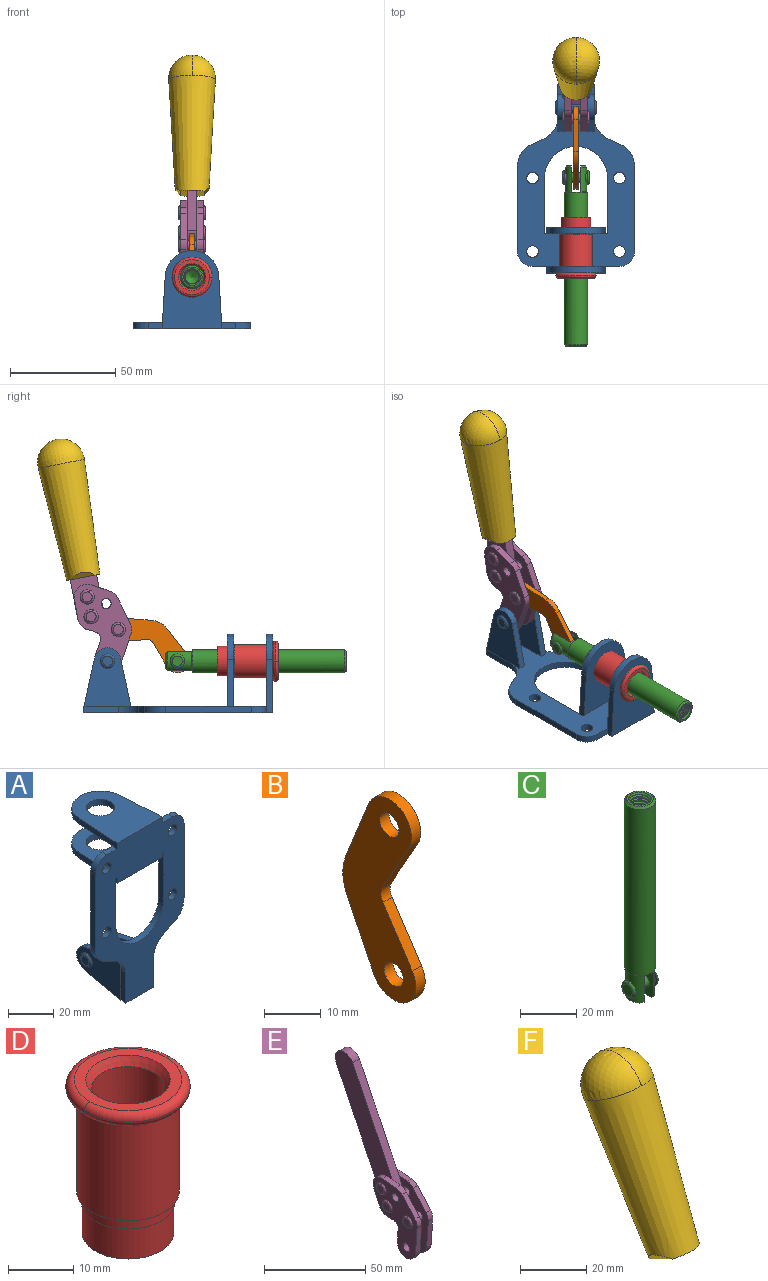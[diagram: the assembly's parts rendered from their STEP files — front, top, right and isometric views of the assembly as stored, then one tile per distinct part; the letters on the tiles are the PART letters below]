
ASSEMBLY  parts=6 mates=6
PART A: 55 faces, bbox 55.7x37.4x89.8 mm
  f0: torus R=2.41mm, axis (-1,0,0), area 15mm2, adj f11,f15,f25
  f1: torus R=2.41mm, axis (-1,0,0), area 15mm2, adj f10,f12,f22
  f2: cylinder r=2.78mm len=5.56mm, axis (0,-1,0), area 54.2mm2, adj f30,f54
  f3: cylinder r=14.99mm len=29.97mm, axis (0,-1,0), area 145.9mm2, adj f30,f49,f53,f54
  f4: cylinder r=2.78mm len=5.56mm, axis (0,-1,0), area 54.2mm2, adj f30,f54
  f5: cylinder r=2.78mm len=5.56mm, axis (0,-1,0), area 54.2mm2, adj f30,f54
  f6: cylinder r=2.78mm len=5.56mm, axis (0,-1,0), area 54.2mm2, adj f30,f54
  f7: cylinder r=6.35mm len=12.7mm, axis (0,0,1), area 123.6mm2, adj f27,f51
  f8: cylinder r=6.35mm len=12.7mm, axis (0,0,-1), area 124.7mm2, adj f21,f35
  f9: cylinder r=2.41mm len=11.18mm, axis (-1,0,0), area 169.4mm2, adj f16,f19
  f10: plane 4.83x4.83mm, normal (1,0,0), area 18.3mm2, adj f1,f12
  f11: plane 4.83x4.83mm, normal (-1,0,0), area 18.3mm2, adj f0,f15
  f12: torus R=2.41mm, axis (-1,0,0), area 15mm2, adj f1,f10,f22
  f13: cylinder r=6.35mm len=12.41mm, axis (1,0,0), area 53.4mm2, adj f18,f19,f22,f23
  f14: cylinder r=6.35mm len=12.41mm, axis (-1,0,0), area 53.4mm2, adj f16,f17,f24,f25
  f15: torus R=2.41mm, axis (-1,0,0), area 15mm2, adj f0,f11,f25
  f16: plane 27.86x22.35mm, normal (1,0,0), area 425.4mm2, adj f9,f14,f17,f24,f30
  f17: plane 22.86x4.97mm, normal (0,0.21,0.98), area 72.5mm2, adj f14,f16,f25,f30
  f18: plane 22.86x4.97mm, normal (0,0.21,0.98), area 72.5mm2, adj f13,f19,f22,f30
  f19: plane 27.86x22.35mm, normal (-1,0,0), area 425.4mm2, adj f9,f13,f18,f23,f30
  f20: cylinder r=12.7mm len=25.35mm, axis (0,0,-1), area 119.8mm2, adj f21,f34,f35,f36
  f21: plane 34.21x28.07mm, normal (0,0,-1), area 702.4mm2, adj f8,f20,f30,f34,f36
  f22: plane 27.96x22.45mm, normal (1,0,0), area 407.2mm2, adj f1,f12,f13,f18,f23,f30,f42,f43
  f23: plane 22.86x4.97mm, normal (0,0.21,-0.98), area 72.5mm2, adj f13,f19,f22,f44
  f24: plane 22.86x4.97mm, normal (0,0.21,-0.98), area 72.5mm2, adj f14,f16,f25,f44
  f25: plane 27.86x22.35mm, normal (-1,0,0), area 407.1mm2, adj f0,f14,f15,f17,f24,f30,f45,f46
  f26: plane 3.1x0.95mm, normal (0,0,-1), area 2.7mm2, adj f30,f49,f50,f54
  f27: plane 34.21x28.07mm, normal (0,0,1), area 702.4mm2, adj f7,f28,f30,f50,f52
  f28: cylinder r=12.7mm len=25.35mm, axis (0,0,1), area 118.8mm2, adj f27,f50,f51,f52
  f29: plane 3.1x0.95mm, normal (0,0,-1), area 2.7mm2, adj f30,f52,f53,f54
  f30: plane 86.54x55.63mm, normal (0,1,0), area 2362.9mm2, adj f2,f3,f4,f5,f6,f16,f17,f18
  f31: plane 40.56x3.1mm, normal (-1,0,0), area 125.7mm2, adj f30,f32,f48,f54
  f32: cylinder r=7.11mm len=7.11mm, axis (0,-1,0), area 34.6mm2, adj f30,f31,f33,f54
  f33: plane 6.67x3.1mm, normal (0,0,1), area 20.4mm2, adj f30,f32,f34,f54
  f34: plane 25.39x3.13mm, normal (-1,0.06,0), area 79.5mm2, adj f20,f21,f33,f35,f54
  f35: plane 37.31x28.45mm, normal (0,0,1), area 789.9mm2, adj f8,f20,f34,f36,f54
  f36: plane 25.39x3.13mm, normal (1,0.06,0), area 79.5mm2, adj f20,f21,f35,f37,f54
  f37: plane 6.67x3.1mm, normal (0,0,1), area 20.4mm2, adj f30,f36,f38,f54
  f38: cylinder r=7.11mm len=7.11mm, axis (0,-1,0), area 34.6mm2, adj f30,f37,f39,f54
  f39: plane 40.56x3.1mm, normal (1,0,0), area 125.7mm2, adj f30,f38,f40,f54
  f40: cylinder r=11.18mm len=10.16mm, axis (0,-1,0), area 39.5mm2, adj f30,f39,f41,f54
  f41: plane 6.09x3.1mm, normal (0.42,0,-0.91), area 20.8mm2, adj f30,f40,f42,f54
  f42: cylinder r=11.18mm len=9.41mm, axis (0,-1,0), area 37.2mm2, adj f22,f30,f41,f43,f54
  f43: plane 16.5x3.1mm, normal (1,0,0), area 51.1mm2, adj f22,f42,f44,f54
  f44: plane 17.37x3.1mm, normal (0,0,-1), area 53.8mm2, adj f23,f24,f30,f43,f45,f54
  f45: plane 16.5x3.1mm, normal (-1,0,0), area 51.1mm2, adj f25,f44,f46,f54
  f46: cylinder r=11.18mm len=9.41mm, axis (0,-1,0), area 37.2mm2, adj f25,f30,f45,f47,f54
  f47: plane 6.09x3.1mm, normal (-0.42,0,-0.91), area 20.8mm2, adj f30,f46,f48,f54
  f48: cylinder r=11.18mm len=10.16mm, axis (0,-1,0), area 39.5mm2, adj f30,f31,f47,f54
  f49: plane 26.54x3.1mm, normal (-1,0,0), area 82.3mm2, adj f3,f26,f30,f54
  f50: plane 25.39x3.1mm, normal (1,0.06,0), area 78.8mm2, adj f26,f27,f28,f51,f54
  f51: plane 37.31x28.45mm, normal (0,0,-1), area 789.9mm2, adj f7,f28,f50,f52,f54
  f52: plane 25.39x3.1mm, normal (-1,0.06,0), area 78.8mm2, adj f27,f28,f29,f51,f54
  f53: plane 26.54x3.1mm, normal (1,0,0), area 82.3mm2, adj f3,f29,f30,f54
  f54: plane 89.66x55.63mm, normal (0,-1,0), area 2678.5mm2, adj f2,f3,f4,f5,f6,f26,f29,f31
PART B: 12 faces, bbox 2.3x18.2x42.8 mm
  f0: cylinder r=2.4mm len=4.8mm, axis (1,0,0), area 34.9mm2, adj f4,f11
  f1: cylinder r=10.41mm len=8.47mm, axis (1,0,0), area 20.2mm2, adj f4,f9,f10,f11
  f2: cylinder r=3.05mm len=3.16mm, axis (1,0,0), area 7.7mm2, adj f4,f6,f7,f11
  f3: cylinder r=2.4mm len=4.8mm, axis (1,0,0), area 34.9mm2, adj f4,f11
  f4: plane 42.81x18.23mm, normal (-1,0,0), area 414.1mm2, adj f0,f1,f2,f3,f5,f6,f7,f8
  f5: cylinder r=5.54mm len=10.67mm, axis (1,0,0), area 41.8mm2, adj f4,f6,f10,f11
  f6: plane 11.66x6.53mm, normal (0,-0.87,-0.49), area 30.9mm2, adj f2,f4,f5,f11
  f7: plane 11.17x7.33mm, normal (0,-0.84,0.55), area 30.9mm2, adj f2,f4,f8,f11
  f8: cylinder r=5.54mm len=10.51mm, axis (1,0,0), area 41.8mm2, adj f4,f7,f9,f11
  f9: plane 13.67x6.67mm, normal (0,0.9,-0.44), area 35.1mm2, adj f1,f4,f8,f11
  f10: plane 14.1x5.7mm, normal (0,0.93,0.37), area 35.1mm2, adj f1,f4,f5,f11
  f11: plane 42.81x18.23mm, normal (1,0,0), area 414.1mm2, adj f0,f1,f2,f3,f5,f6,f7,f8
PART C: 48 faces, bbox 12.6x11.1x86.1 mm
  f0: torus R=2.41mm, axis (-1,0,0), area 15mm2, adj f30,f32,f34
  f1: torus R=2.41mm, axis (-1,0,0), area 15mm2, adj f29,f31,f33
  f2: cylinder r=5.54mm len=72.39mm, axis (0,0,1), area 2518.5mm2, adj f3,f4,f42,f43
  f3: cone r=5.54mm half-angle=45deg, axis (0,0,1), area 7.6mm2, adj f2,f5,f41
  f4: cone r=5.54mm half-angle=45deg, axis (0,0,-1), area 34.9mm2, adj f2,f39
  f5: cylinder r=5.08mm len=11.48mm, axis (0,0,1), area 108.3mm2, adj f3,f7,f8,f41
  f6: cylinder r=2.41mm len=4.83mm, axis (-1,0,0), area 71.2mm2, adj f40,f41
  f7: cylinder r=2.41mm len=4.83mm, axis (-1,0,0), area 7.6mm2, adj f5,f34
  f8: cone r=5.08mm half-angle=45deg, axis (0,0,1), area 10.6mm2, adj f5,f37,f41
  f9: cone r=3.98mm half-angle=45deg, axis (0,0,1), area 17.6mm2, adj f27,f39,f45,f46,f47
  f10: cylinder r=2.41mm len=4.83mm, axis (-1,0,0), area 7.6mm2, adj f33,f38
  f11: cylinder r=3.2mm len=6.4mm, axis (0,0,1), area 78.4mm2, adj f12,f28,f44,f45,f47
  f12: cylinder r=3.2mm len=6.4mm, axis (0,0,1), area 10.5mm2, adj f11,f13,f45,f47
  f13: cylinder r=3.2mm len=6.4mm, axis (0,0,1), area 10.5mm2, adj f12,f14,f45,f47
  f14: cylinder r=3.2mm len=6.4mm, axis (0,0,1), area 10.5mm2, adj f13,f15,f45,f47
  f15: cylinder r=3.2mm len=6.4mm, axis (0,0,1), area 10.5mm2, adj f14,f16,f45,f47
  f16: cylinder r=3.2mm len=6.4mm, axis (0,0,1), area 10.5mm2, adj f15,f17,f45,f47
  f17: cylinder r=3.2mm len=6.4mm, axis (0,0,1), area 10.5mm2, adj f16,f18,f45,f47
  f18: cylinder r=3.2mm len=6.4mm, axis (0,0,1), area 10.5mm2, adj f17,f19,f45,f47
  f19: cylinder r=3.2mm len=6.4mm, axis (0,0,1), area 10.5mm2, adj f18,f20,f45,f47
  f20: cylinder r=3.2mm len=6.4mm, axis (0,0,1), area 10.5mm2, adj f19,f21,f45,f47
  f21: cylinder r=3.2mm len=6.4mm, axis (0,0,1), area 10.5mm2, adj f20,f22,f45,f47
  f22: cylinder r=3.2mm len=6.4mm, axis (0,0,1), area 10.5mm2, adj f21,f23,f45,f47
  f23: cylinder r=3.2mm len=6.4mm, axis (0,0,1), area 10.5mm2, adj f22,f24,f45,f47
  f24: cylinder r=3.2mm len=6.4mm, axis (0,0,1), area 10.5mm2, adj f23,f25,f45,f47
  f25: cylinder r=3.2mm len=6.4mm, axis (0,0,1), area 10.5mm2, adj f24,f26,f45,f47
  f26: cylinder r=3.2mm len=6.4mm, axis (0,0,1), area 10.5mm2, adj f25,f27,f45,f47
  f27: cylinder r=3.2mm len=6.4mm, axis (0,0,1), area 7.4mm2, adj f9,f26,f45,f47
  f28: cone r=3.2mm half-angle=60deg, axis (0,0,1), area 37.2mm2, adj f11
  f29: plane 4.83x4.83mm, normal (-1,0,0), area 18.3mm2, adj f1,f31
  f30: plane 4.83x4.83mm, normal (1,0,0), area 18.3mm2, adj f0,f32
  f31: torus R=2.41mm, axis (-1,0,0), area 15mm2, adj f1,f29,f33
  f32: torus R=2.41mm, axis (-1,0,0), area 15mm2, adj f0,f30,f34
  f33: plane 6.83x6.83mm, normal (1,0,0), area 18.3mm2, adj f1,f10,f31
  f34: plane 6.83x6.83mm, normal (-1,0,0), area 18.3mm2, adj f0,f7,f32
  f35: cone r=5.08mm half-angle=45deg, axis (0,0,1), area 10.6mm2, adj f36,f38,f40
  f36: plane 7.25x1.97mm, normal (0,0,-1), area 10mm2, adj f35,f40
  f37: plane 7.25x1.97mm, normal (0,0,-1), area 10mm2, adj f8,f41
  f38: cylinder r=5.08mm len=11.48mm, axis (0,0,1), area 108.3mm2, adj f10,f35,f40,f42
  f39: plane 9.55x9.55mm, normal (0,0,1), area 22mm2, adj f4,f9
  f40: plane 12.76x10.09mm, normal (1,0,0), area 95.7mm2, adj f6,f35,f36,f38,f42,f43
  f41: plane 12.76x10.09mm, normal (-1,0,0), area 95.7mm2, adj f3,f5,f6,f8,f37,f43
  f42: cone r=5.54mm half-angle=45deg, axis (0,0,1), area 7.6mm2, adj f2,f38,f40
  f43: plane 11.07x4.7mm, normal (0,0,-1), area 50.4mm2, adj f2,f40,f41
  f44: plane 0.89x0.62mm, normal (-1,0,0), area 0.3mm2, adj f11,f45,f46,f47
  f45: bspline ~24.8x7.63mm, area 266.6mm2, adj f9,f11,f12,f13,f14,f15,f16,f17
  f46: bspline ~24.87x7.63mm, area 73.6mm2, adj f9,f44,f45,f47
  f47: bspline ~24.98x7.63mm, area 272.5mm2, adj f9,f11,f12,f13,f14,f15,f16,f17
PART D: 15 faces, bbox 20.6x20.6x28.7 mm
  f0: torus R=8.26mm, axis (0,0,1), area 56.8mm2, adj f1,f10,f12
  f1: torus R=8.26mm, axis (0,0,1), area 56.8mm2, adj f0,f6,f13
  f2: cylinder r=5.59mm len=25.91mm, axis (0,0,1), area 909.6mm2, adj f3,f4
  f3: cone r=6.86mm half-angle=45deg, axis (0,0,-1), area 70.2mm2, adj f2,f14
  f4: cone r=6.47mm half-angle=30deg, axis (0,0,1), area 66.7mm2, adj f2,f13
  f5: cylinder r=7.04mm len=14.07mm, axis (0,0,1), area 252.6mm2, adj f11,f14
  f6: torus R=8.26mm, axis (0,0,1), area 56.8mm2, adj f1,f12,f13
  f7: cylinder r=7.16mm len=14.33mm, axis (0,0,1), area 91.5mm2, adj f9,f11
  f8: cylinder r=7.86mm len=18.42mm, axis (0,0,1), area 909.6mm2, adj f9,f10
  f9: plane 15.72x15.72mm, normal (0,0,-1), area 33mm2, adj f7,f8
  f10: plane 16.51x16.51mm, normal (0,0,-1), area 19.9mm2, adj f0,f8,f12
  f11: plane 14.33x14.33mm, normal (0,0,-1), area 5.7mm2, adj f5,f7
  f12: torus R=8.26mm, axis (0,0,1), area 56.8mm2, adj f0,f6,f10
  f13: plane 16.51x16.51mm, normal (0,0,1), area 82.7mm2, adj f1,f4,f6
  f14: plane 14.07x14.07mm, normal (0,0,-1), area 7.8mm2, adj f3,f5
PART E: 59 faces, bbox 12.9x60.2x99.6 mm
  f0: torus R=2.39mm, axis (-1,0,0), area 14.9mm2, adj f20,f43,f51
  f1: torus R=2.39mm, axis (-1,0,0), area 14.9mm2, adj f19,f42,f51
  f2: torus R=2.39mm, axis (-1,0,0), area 14.9mm2, adj f18,f35,f51
  f3: torus R=2.39mm, axis (-1,0,0), area 14.9mm2, adj f14,f17,f23
  f4: torus R=2.39mm, axis (-1,0,0), area 14.9mm2, adj f13,f16,f23
  f5: torus R=2.39mm, axis (-1,0,0), area 14.9mm2, adj f12,f15,f23
  f6: cylinder r=2.39mm len=4.78mm, axis (1,0,0), area 46.5mm2, adj f48,f50,f51
  f7: cylinder r=2.39mm len=4.78mm, axis (1,0,0), area 46.5mm2, adj f50,f51
  f8: cylinder r=6.35mm len=12.68mm, axis (1,0,0), area 61.8mm2, adj f38,f39,f50,f51
  f9: cylinder r=2.39mm len=4.78mm, axis (-1,0,0), area 70.5mm2, adj f46,f50
  f10: cylinder r=2.39mm len=4.78mm, axis (-1,0,0), area 46.5mm2, adj f23,f45,f46
  f11: cylinder r=2.39mm len=4.78mm, axis (-1,0,0), area 46.5mm2, adj f23,f46
  f12: plane 4.78x4.78mm, normal (1,0,0), area 17.9mm2, adj f5,f15
  f13: plane 4.78x4.78mm, normal (1,0,0), area 17.9mm2, adj f4,f16
  f14: plane 4.78x4.78mm, normal (1,0,0), area 17.9mm2, adj f3,f17
  f15: torus R=2.39mm, axis (-1,0,0), area 14.9mm2, adj f5,f12,f23
  f16: torus R=2.39mm, axis (-1,0,0), area 14.9mm2, adj f4,f13,f23
  f17: torus R=2.39mm, axis (-1,0,0), area 14.9mm2, adj f3,f14,f23
  f18: plane 4.78x4.78mm, normal (-1,0,0), area 17.9mm2, adj f2,f35
  f19: plane 4.78x4.78mm, normal (-1,0,0), area 17.9mm2, adj f1,f42
  f20: plane 4.78x4.78mm, normal (-1,0,0), area 17.9mm2, adj f0,f43
  f21: plane 2.26x0.2mm, normal (1,0,0), area 0.2mm2, adj f31,f44
  f22: plane 2.26x0.2mm, normal (-1,0,0), area 0.2mm2, adj f41,f44
  f23: plane 39.37x30.77mm, normal (1,0,0), area 565.5mm2, adj f3,f4,f5,f10,f11,f15,f16,f17
  f24: cylinder r=6.1mm len=4.15mm, axis (-1,0,0), area 14.7mm2, adj f23,f25,f32,f46
  f25: plane 10.25x9.01mm, normal (0,-0.75,0.66), area 42.3mm2, adj f23,f24,f26,f46
  f26: cylinder r=6.35mm len=4.64mm, axis (-1,0,0), area 15.6mm2, adj f23,f25,f27,f46
  f27: plane 15.84x3.1mm, normal (0,-1,-0.07), area 49.2mm2, adj f23,f26,f28,f46
  f28: cylinder r=6.35mm len=12.68mm, axis (-1,0,0), area 61.8mm2, adj f23,f27,f29,f46
  f29: plane 8.11x3.1mm, normal (0,1,0.07), area 25.2mm2, adj f23,f28,f30,f46
  f30: cylinder r=3.05mm len=3.25mm, axis (-1,0,0), area 14.8mm2, adj f23,f29,f31,f46
  f31: plane 5.99x3.1mm, normal (0,0.07,-1), area 18.6mm2, adj f21,f23,f30,f44,f46
  f32: plane 9.5x3.1mm, normal (0,-0.07,1), area 29.5mm2, adj f23,f24,f33,f46,f47
  f33: cylinder r=6.1mm len=8.63mm, axis (-1,0,0), area 39.1mm2, adj f23,f32,f34,f47
  f34: plane 8.65x3.96mm, normal (0,0.91,-0.42), area 29.5mm2, adj f23,f33,f44,f47
  f35: torus R=2.39mm, axis (-1,0,0), area 14.9mm2, adj f2,f18,f51
  f36: plane 10.25x9.01mm, normal (0,-0.75,0.66), area 42.3mm2, adj f37,f49,f50,f51
  f37: cylinder r=6.35mm len=4.64mm, axis (1,0,0), area 15.6mm2, adj f36,f38,f50,f51
  f38: plane 15.84x3.1mm, normal (0,-1,-0.07), area 49.2mm2, adj f8,f37,f50,f51
  f39: plane 8.11x3.1mm, normal (0,1,0.07), area 25.2mm2, adj f8,f40,f50,f51
  f40: cylinder r=3.05mm len=3.25mm, axis (1,0,0), area 14.8mm2, adj f39,f41,f50,f51
  f41: plane 5.99x3.1mm, normal (0,0.07,-1), area 18.6mm2, adj f22,f40,f44,f50,f51
  f42: torus R=2.39mm, axis (-1,0,0), area 14.9mm2, adj f1,f19,f51
  f43: torus R=2.39mm, axis (-1,0,0), area 14.9mm2, adj f0,f20,f51
  f44: cylinder r=6.35mm len=12.12mm, axis (-1,0,0), area 128.9mm2, adj f21,f22,f23,f31,f34,f41,f46,f47
  f45: plane 2.65x1.35mm, normal (1,0,0), area 1mm2, adj f10,f55
  f46: plane 39.08x20.42mm, normal (-1,0,0), area 412.5mm2, adj f9,f10,f11,f24,f25,f26,f27,f28
  f47: plane 77.62x39.82mm, normal (1,0,0), area 850mm2, adj f32,f33,f34,f44,f53,f54,f55
  f48: plane 2.65x1.35mm, normal (-1,0,0), area 1mm2, adj f6,f55
  f49: cylinder r=6.1mm len=4.15mm, axis (1,0,0), area 14.7mm2, adj f36,f50,f51,f56
  f50: plane 39.08x20.42mm, normal (1,0,0), area 412.5mm2, adj f6,f7,f8,f9,f36,f37,f38,f39
  f51: plane 39.37x30.77mm, normal (-1,0,0), area 565.5mm2, adj f0,f1,f2,f6,f7,f8,f35,f36
  f52: plane 8.65x3.96mm, normal (0,0.91,-0.42), area 29.5mm2, adj f44,f51,f57,f58
  f53: plane 68.49x33.4mm, normal (0,0.9,-0.44), area 358.1mm2, adj f44,f47,f54,f58
  f54: cylinder r=6.35mm len=12.06mm, axis (1,0,0), area 93.7mm2, adj f47,f53,f55,f58
  f55: plane 68.49x33.4mm, normal (0,-0.9,0.44), area 358.1mm2, adj f44,f45,f46,f47,f48,f50,f54,f58
  f56: plane 9.5x3.1mm, normal (0,-0.07,1), area 29.5mm2, adj f49,f50,f51,f57,f58
  f57: cylinder r=6.1mm len=8.63mm, axis (1,0,0), area 39.1mm2, adj f51,f52,f56,f58
  f58: plane 77.62x39.82mm, normal (-1,0,0), area 850mm2, adj f44,f52,f53,f54,f55,f56,f57
PART F: 11 faces, bbox 22.3x42.6x64.5 mm
  f0: sphere r=11.13mm, area 411.4mm2, adj f1,f8
  f1: cone r=11.11mm half-angle=3.3deg, axis (0,0.44,0.9), area 3251.8mm2, adj f0,f7,f8,f9,f10
  f2: cylinder r=6.16mm len=11.7mm, axis (1,0,0), area 89.5mm2, adj f3,f4,f5,f6
  f3: plane 60.23x36.75mm, normal (-1,0,0), area 763.6mm2, adj f2,f4,f6,f10
  f4: plane 51.37x25.05mm, normal (0,0.9,-0.44), area 264.2mm2, adj f2,f3,f5,f10
  f5: plane 60.23x36.75mm, normal (1,0,0), area 763.6mm2, adj f2,f4,f6,f10
  f6: plane 51.37x25.05mm, normal (0,-0.9,0.44), area 264.2mm2, adj f2,f3,f5,f10
  f7: plane 9.95x5.95mm, normal (0.71,-0.31,-0.64), area 25.8mm2, adj f1,f10
  f8: sphere r=11.13mm, area 411.4mm2, adj f0,f1
  f9: plane 9.95x5.95mm, normal (-0.71,-0.31,-0.64), area 25.8mm2, adj f1,f10
  f10: plane 14.27x11.38mm, normal (0,-0.44,-0.9), area 106.7mm2, adj f1,f3,f4,f5,f6,f7,f9
PLACE A rot(axis=(1,0,0),90deg) t=(0,1.23,0)mm fixed
PLACE B rot(axis=(0,-0.53,-0.85),180deg) t=(0,25.15,10.71)mm
PLACE C rot(axis=(1,0,0),90deg) t=(0,15.65,0)mm
PLACE D rot(axis=(1,0,0),90deg) t=(0,1.23,0)mm
PLACE E rot(axis=(1,0,0),15deg) t=(0,1.24,49.24)mm
PLACE F rot(axis=(1,0,0),15deg) t=(0.04,1.24,49.24)mm
MATE revolute E.f7 <-> A.f0  axis (-1,0,0) through (0,33.32,24.61)mm
MATE revolute B.f3 <-> C.f6  axis (-1,0,0) through (0,0.18,24.61)mm
MATE fastened E.f54 <-> F.f2  axis (1,0,0) through (2.35,55.69,120.54)mm
MATE fastened A.f7 <-> D.f2  axis (0,1,0) through (0,-45.16,24.61)mm
MATE slider A.f7 <-> C.f2  axis (0,-1,0) through (0,-45.16,24.61)mm
MATE revolute B.f5 <-> E.f4  axis (-1,0,0) through (0,28.16,39.62)mm
